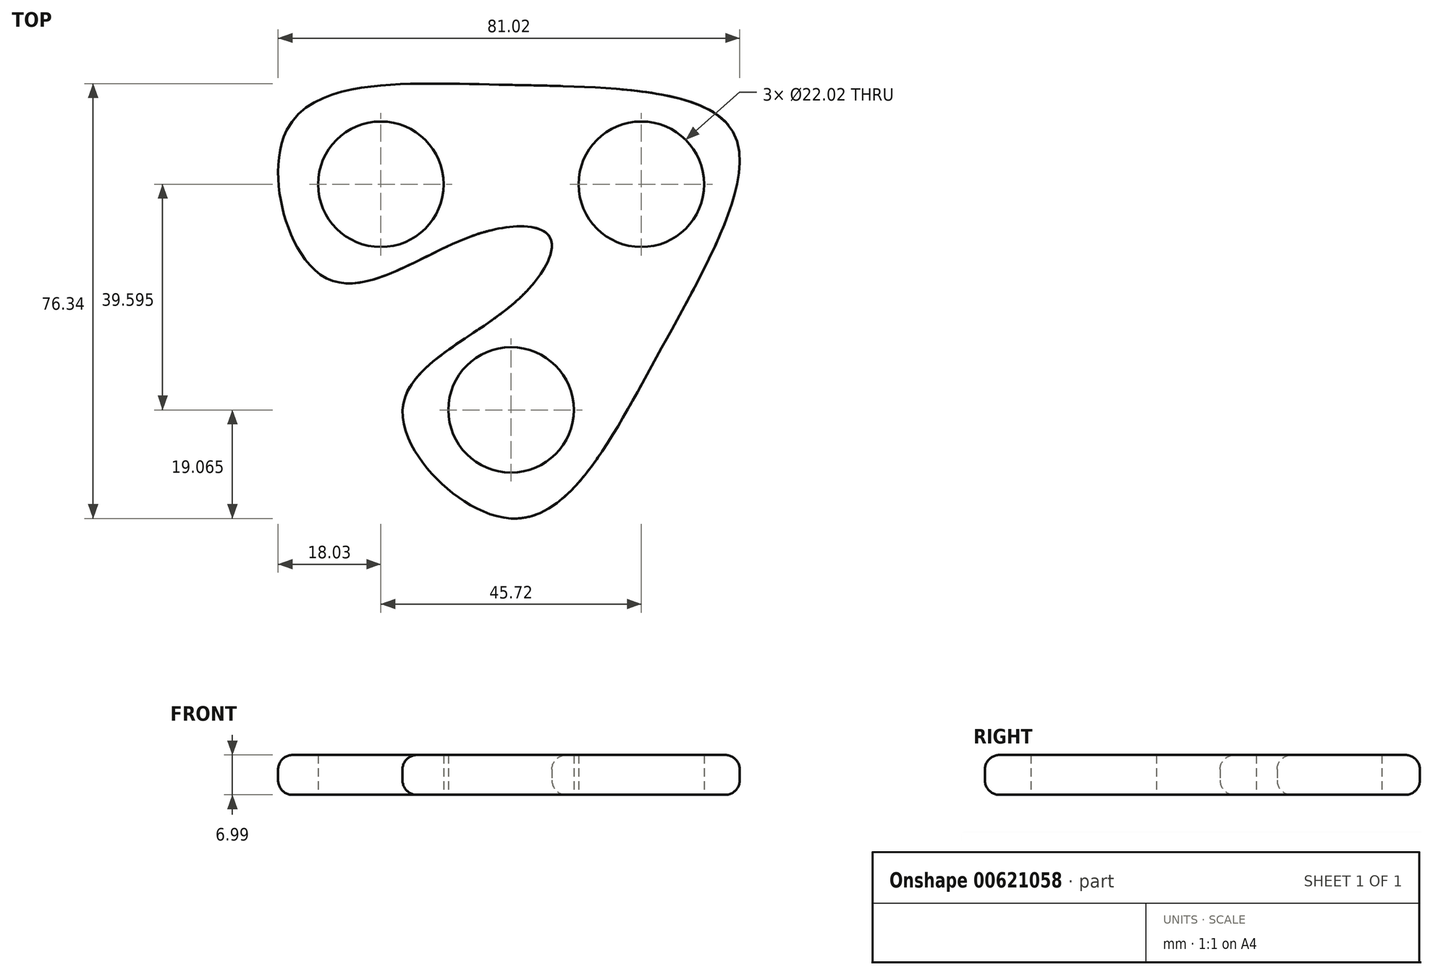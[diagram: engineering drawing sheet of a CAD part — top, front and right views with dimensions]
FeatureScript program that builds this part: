
annotation { "Feature Type Name" : "Feature", "Feature Type Description" : "" }
export const myFeature = defineFeature(function(context is Context, id is Id, definition is map)
    precondition{}
    {
        {
            var Q0;
            Q0=qCreatedBy(makeId("Top.planeOp"),FACE);
            var sketch = newSketch(context, id + "F0", { "sketchPlane" : qUnion([Q0])});
            skFitSpline(sketch, "E0", {"points": [v(-62.22, 9.52) * mm, v(-24.97, 17.48) * mm, v(16.06, 9.27) * mm, v(2.66, -30.36) * mm, v(-22.86, -58.64) * mm, v(-41.91, -39.6) * mm, v(-22.86, -21.3) * mm, v(-16.06, -9.27) * mm, v(-29.88, -9.14) * mm, v(-55.25, -16.5) * mm, v(-62.22, 9.52) * mm]});
            skCircle(sketch, "E1", {"center": v(0, 0) * mm, "radius": 11.01 * mm});
            skCircle(sketch, "E2", {"center": v(-45.72, 0) * mm, "radius": 11.01 * mm});
            skCircle(sketch, "E3", {"center": v(-22.86, -39.6) * mm, "radius": 11.01 * mm});
            skLineSegment(sketch, "E4", {"start": v(-22.86, -39.6) * mm, "end": v(0, 0) * mm});
            skLineSegment(sketch, "E5", {"start": v(-45.72, 0) * mm, "end": v(0, 0) * mm});
            skLineSegment(sketch, "E6", {"start": v(-45.72, 0) * mm, "end": v(-62.22, 9.52) * mm});
            skLineSegment(sketch, "E7", {"start": v(-45.72, 0) * mm, "end": v(-55.25, -16.5) * mm});
            skLineSegment(sketch, "E8", {"start": v(-22.86, -39.6) * mm, "end": v(-41.91, -39.6) * mm});
            skLineSegment(sketch, "E9", {"start": v(-22.86, -39.6) * mm, "end": v(-22.86, -58.64) * mm});
            skLineSegment(sketch, "E10", {"start": v(0, 0) * mm, "end": v(-16.06, -9.27) * mm});
            skLineSegment(sketch, "E11", {"start": v(0, 0) * mm, "end": v(16.06, 9.27) * mm});
            skLineSegment(sketch, "E12", {"start": v(-45.72, 0) * mm, "end": v(-29.88, -9.14) * mm});
            skLineSegment(sketch, "E13", {"start": v(-22.86, -39.6) * mm, "end": v(-22.86, -21.3) * mm});
            skLineSegment(sketch, "E14", {"start": v(0, 0) * mm, "end": v(-24.97, 17.48) * mm});
            skLineSegment(sketch, "E15", {"start": v(0, 0) * mm, "end": v(2.66, -30.36) * mm});
            skSolve(sketch);
        }
        {
            var Q0;
            Q0 = qSketchRegion(id + "F0", true);
            extrude(context, id + "F1", {"entities" : qUnion([Q0]), "depth" : 7 * mm, "offsetDistance" : 25.4 * mm});
        }
        {
            var Q0;
            Q0=makeQuery(id+"F1.opExtrude","CAP_EDGE",EDGE,{"disambiguationData":[OSD([sQuery(id+"F0.wireOp",EDGE,"E0")])],"isStart":true});
            var Q1;
            Q1=makeQuery(id+"F1.opExtrude","CAP_EDGE",EDGE,{"disambiguationData":[OSD([sQuery(id+"F0.wireOp",EDGE,"E0")])],"isStart":false});
            fillet(context, id + "F2", {"entities" : qUnion([Q0, Q1]), "radius" : 2.54 * mm, "tangentPropagation" : true, "allowEdgeOverflow" : false});
        }
    });
